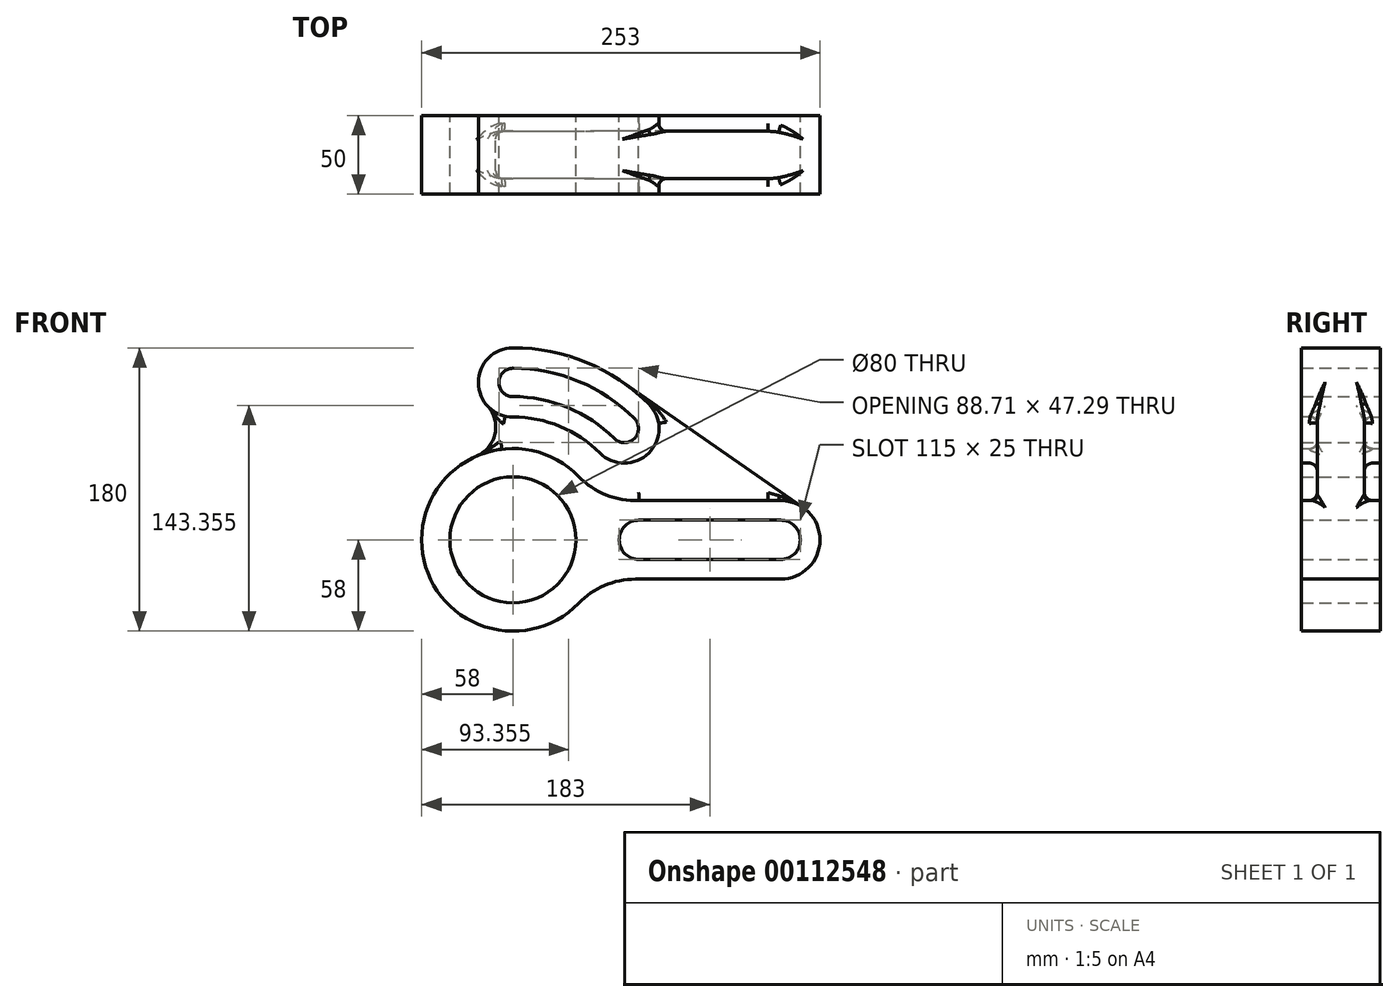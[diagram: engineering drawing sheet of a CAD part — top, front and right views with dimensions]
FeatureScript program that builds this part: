
annotation { "Feature Type Name" : "Feature", "Feature Type Description" : "" }
export const myFeature = defineFeature(function(context is Context, id is Id, definition is map)
    precondition{}
    {
        {
            var Q0;
            Q0=qCreatedBy(makeId("Front.planeOp"),FACE);
            var sketch = newSketch(context, id + "F0", { "sketchPlane" : qUnion([Q0])});
            skCircle(sketch, "E0", {"center": v(0, 0) * mm, "radius": 40 * mm});
            skCircle(sketch, "E1", {"center": v(0, 0) * mm, "radius": 58 * mm});
            skArc(sketch, "E2", {"start": v(-23, 53.24) * mm, "mid": v(-11.38, 67.43) * mm, "end": v(-16.2, 85.12) * mm});
            skArc(sketch, "E3", {"start": v(0, 122) * mm, "mid": v(-20.14, 108.85) * mm, "end": v(-16.2, 85.12) * mm});
            skArc(sketch, "E4", {"start": v(69.61, 100.2) * mm, "mid": v(36.47, 116.42) * mm, "end": v(0, 122) * mm});
            skLineSegment(sketch, "E5", {"start": v(69.61, 100.2) * mm, "end": v(184.26, 20.53) * mm});
            skArc(sketch, "E6", {"start": v(170, -25) * mm, "mid": v(193.86, -7.47) * mm, "end": v(184.26, 20.53) * mm});
            skLineSegment(sketch, "E7", {"start": v(170, -25) * mm, "end": v(77.71, -25) * mm});
            skArc(sketch, "E8", {"start": v(77.71, -25) * mm, "mid": v(58.17, -28.98) * mm, "end": v(41.73, -40.28) * mm});
            skCircle(sketch, "E9", {"center": v(0, 0) * mm, "radius": 100 * mm, "construction": true});
            skArc(sketch, "E10", {"start": v(0, 109) * mm, "mid": v(-9, 100) * mm, "end": v(0, 91) * mm});
            skArc(sketch, "E11.0", {"start": v(77.07, 77.07) * mm, "mid": v(41.71, 100.7) * mm, "end": v(0, 109) * mm});
            skArc(sketch, "E12.0", {"start": v(64.35, 64.35) * mm, "mid": v(34.82, 84.07) * mm, "end": v(0, 91) * mm});
            skArc(sketch, "E13", {"start": v(64.35, 64.35) * mm, "mid": v(77.07, 64.35) * mm, "end": v(77.07, 77.07) * mm});
            skLineSegment(sketch, "E14", {"start": v(0, 0) * mm, "end": v(0, 158.86) * mm, "construction": true});
            skLineSegment(sketch, "E15", {"start": v(0, 0) * mm, "end": v(114.9, 114.9) * mm, "construction": true});
            skArc(sketch, "E16", {"start": v(170, -12.5) * mm, "mid": v(182.5, 0) * mm, "end": v(170, 12.5) * mm});
            skArc(sketch, "E17", {"start": v(80, 12.5) * mm, "mid": v(67.5, 0) * mm, "end": v(80, -12.5) * mm});
            skLineSegment(sketch, "E18", {"start": v(80, 12.5) * mm, "end": v(170, 12.5) * mm});
            skLineSegment(sketch, "E19", {"start": v(80, -12.5) * mm, "end": v(170, -12.5) * mm});
            skSolve(sketch);
        }
        {
            var Q0;
            Q0 = qSketchRegion(id + "F0", true);
            extrude(context, id + "F1", {"entities" : qUnion([Q0]), "depth" : 50 * mm});
        }
        {
            var Q0;
            Q0=makeQuery(id+"F1.opExtrude","CAP_FACE",FACE,{"disambiguationData":[OSD([sQuery(id+"F0.wireOp",EDGE,"E0"),sQuery(id+"F0.wireOp",EDGE,"E1"),sQuery(id+"F0.wireOp",EDGE,"E2"),sQuery(id+"F0.wireOp",EDGE,"E3"),sQuery(id+"F0.wireOp",EDGE,"E4"),sQuery(id+"F0.wireOp",EDGE,"E5"),sQuery(id+"F0.wireOp",EDGE,"E6"),sQuery(id+"F0.wireOp",EDGE,"E7"),sQuery(id+"F0.wireOp",EDGE,"E8"),sQuery(id+"F0.wireOp",EDGE,"E10"),sQuery(id+"F0.wireOp",EDGE,"E11.0"),sQuery(id+"F0.wireOp",EDGE,"E12.0"),sQuery(id+"F0.wireOp",EDGE,"E13"),sQuery(id+"F0.wireOp",EDGE,"E16"),sQuery(id+"F0.wireOp",EDGE,"E17"),sQuery(id+"F0.wireOp",EDGE,"E18"),sQuery(id+"F0.wireOp",EDGE,"E19")])],"isStart":false});
            var sketch = newSketch(context, id + "F2", { "sketchPlane" : qUnion([Q0])});
            skArc(sketch, "E20.0", {"start": v(-23, 53.24) * mm, "mid": v(-11.38, 67.43) * mm, "end": v(-16.2, 85.12) * mm});
            skArc(sketch, "E21.0", {"start": v(55.15, 55.15) * mm, "mid": v(29.85, 72.06) * mm, "end": v(0, 78) * mm});
            skArc(sketch, "E22", {"start": v(-16.2, 85.12) * mm, "mid": v(-8.85, 79.86) * mm, "end": v(0, 78) * mm, "construction": true});
            skLineSegment(sketch, "E23.1", {"start": v(69.61, 100.2) * mm, "end": v(184.26, 20.53) * mm});
            skArc(sketch, "E24", {"start": v(41.76, 40.25) * mm, "mid": v(11.4, 56.87) * mm, "end": v(-23, 53.24) * mm});
            skArc(sketch, "E25", {"start": v(41.76, 40.25) * mm, "mid": v(59.24, 28.5) * mm, "end": v(80, 25) * mm});
            skLineSegment(sketch, "E26", {"start": v(80, 25) * mm, "end": v(170, 25) * mm});
            skCircle(sketch, "E27", {"center": v(170, 0) * mm, "radius": 25 * mm, "construction": true});
            skArc(sketch, "E28", {"start": v(184.26, 20.53) * mm, "mid": v(177.47, 23.86) * mm, "end": v(170, 25) * mm});
            skCircle(sketch, "E29", {"center": v(80, 0) * mm, "radius": 12.5 * mm, "construction": true});
            skPoint(sketch, "E30.0.end.orphan", {"position": v(41.73, -40.28) * mm});
            skPoint(sketch, "E30.0.start.orphan", {"position": v(77.71, -25) * mm});
            skArc(sketch, "E31", {"start": v(-16.2, 85.12) * mm, "mid": v(-8.85, 79.86) * mm, "end": v(0, 78) * mm});
            skArc(sketch, "E32", {"start": v(55.15, 55.15) * mm, "mid": v(86.27, 55.15) * mm, "end": v(86.27, 86.27) * mm});
            skLineSegment(sketch, "E33", {"start": v(0, 0) * mm, "end": v(98.35, 98.35) * mm, "construction": true});
            skArc(sketch, "E34", {"start": v(86.27, 86.27) * mm, "mid": v(78.25, 93.6) * mm, "end": v(69.61, 100.2) * mm});
            skPoint(sketch, "E35.orphan", {"position": v(0, 122) * mm});
            skSolve(sketch);
        }
        {
            var Q0;
            Q0 = qSketchRegion(id + "F2", true);
            extrude(context, id + "F3", {"entities" : qUnion([Q0]), "operationType" : NewBodyOperationType.REMOVE, "oppositeDirection" : true, "depth" : 10 * mm});
        }
        {
            var Q0;
            Q0=makeQuery(id+"F1.opExtrude","CAP_FACE",FACE,{"disambiguationData":[OSD([sQuery(id+"F0.wireOp",EDGE,"E0"),sQuery(id+"F0.wireOp",EDGE,"E1"),sQuery(id+"F0.wireOp",EDGE,"E2"),sQuery(id+"F0.wireOp",EDGE,"E3"),sQuery(id+"F0.wireOp",EDGE,"E4"),sQuery(id+"F0.wireOp",EDGE,"E5"),sQuery(id+"F0.wireOp",EDGE,"E6"),sQuery(id+"F0.wireOp",EDGE,"E7"),sQuery(id+"F0.wireOp",EDGE,"E8"),sQuery(id+"F0.wireOp",EDGE,"E10"),sQuery(id+"F0.wireOp",EDGE,"E11.0"),sQuery(id+"F0.wireOp",EDGE,"E12.0"),sQuery(id+"F0.wireOp",EDGE,"E13"),sQuery(id+"F0.wireOp",EDGE,"E16"),sQuery(id+"F0.wireOp",EDGE,"E17"),sQuery(id+"F0.wireOp",EDGE,"E18"),sQuery(id+"F0.wireOp",EDGE,"E19")])],"isStart":true});
            var sketch = newSketch(context, id + "F4", { "sketchPlane" : qUnion([Q0])});
            skLineSegment(sketch, "E36.17", {"start": v(-80, 25) * mm, "end": v(-170, 25) * mm});
            skArc(sketch, "E36.18", {"start": v(-41.76, 40.25) * mm, "mid": v(-59.24, 28.5) * mm, "end": v(-80, 25) * mm});
            skArc(sketch, "E36.19", {"start": v(-41.76, 40.25) * mm, "mid": v(-11.4, 56.87) * mm, "end": v(23, 53.24) * mm});
            skArc(sketch, "E36.20", {"start": v(23, 53.24) * mm, "mid": v(11.38, 67.43) * mm, "end": v(16.2, 85.12) * mm});
            skArc(sketch, "E36.21", {"start": v(16.2, 85.12) * mm, "mid": v(8.85, 79.86) * mm, "end": v(0, 78) * mm});
            skArc(sketch, "E36.22", {"start": v(-55.15, 55.15) * mm, "mid": v(-29.85, 72.06) * mm, "end": v(0, 78) * mm});
            skArc(sketch, "E36.23", {"start": v(-55.15, 55.15) * mm, "mid": v(-86.27, 55.15) * mm, "end": v(-86.27, 86.27) * mm});
            skPoint(sketch, "E36.24", {"position": v(-86.27, 86.27) * mm});
            skArc(sketch, "E36.25", {"start": v(-86.27, 86.27) * mm, "mid": v(-78.25, 93.6) * mm, "end": v(-69.61, 100.2) * mm});
            skLineSegment(sketch, "E36.26", {"start": v(-69.61, 100.2) * mm, "end": v(-184.26, 20.53) * mm});
            skArc(sketch, "E36.27", {"start": v(-184.26, 20.53) * mm, "mid": v(-177.47, 23.86) * mm, "end": v(-170, 25) * mm});
            skSolve(sketch);
        }
        {
            var Q0;
            Q0 = qSketchRegion(id + "F4", true);
            extrude(context, id + "F5", {"entities" : qUnion([Q0]), "operationType" : NewBodyOperationType.REMOVE, "oppositeDirection" : true, "depth" : 10 * mm});
        }
        {
            var Q0;
            Q0=makeQuery(id+"F5.boolean.opBoolean","COPY",FACE,{"derivedFrom":makeQuery(id+"F5.opExtrude","CAP_FACE",FACE,{"disambiguationData":[OSD([sQuery(id+"F4.wireOp",EDGE,"E36.17"),sQuery(id+"F4.wireOp",EDGE,"E36.18"),sQuery(id+"F4.wireOp",EDGE,"E36.19"),sQuery(id+"F4.wireOp",EDGE,"E36.20"),sQuery(id+"F4.wireOp",EDGE,"E36.21"),sQuery(id+"F4.wireOp",EDGE,"E36.22"),sQuery(id+"F4.wireOp",EDGE,"E36.23"),sQuery(id+"F4.wireOp",EDGE,"E36.25"),sQuery(id+"F4.wireOp",EDGE,"E36.26"),sQuery(id+"F4.wireOp",EDGE,"E36.27")])],"isStart":false})});
            var Q1;
            Q1=makeQuery(id+"F3.boolean.opBoolean","COPY",FACE,{"derivedFrom":makeQuery(id+"F3.opExtrude","CAP_FACE",FACE,{"disambiguationData":[OSD([sQuery(id+"F2.wireOp",EDGE,"E20.0"),sQuery(id+"F2.wireOp",EDGE,"E21.0"),sQuery(id+"F2.wireOp",EDGE,"E23.1"),sQuery(id+"F2.wireOp",EDGE,"E24"),sQuery(id+"F2.wireOp",EDGE,"E25"),sQuery(id+"F2.wireOp",EDGE,"E26"),sQuery(id+"F2.wireOp",EDGE,"E28"),sQuery(id+"F2.wireOp",EDGE,"E31"),sQuery(id+"F2.wireOp",EDGE,"E32"),sQuery(id+"F2.wireOp",EDGE,"E34")])],"isStart":false})});
            fillet(context, id + "F6", {"entities" : qUnion([Q0, Q1]), "radius" : 5 * mm, "tangentPropagation" : true, "allowEdgeOverflow" : false});
        }
    });
